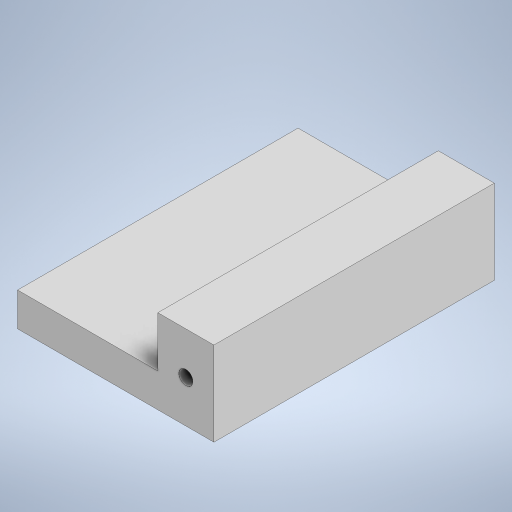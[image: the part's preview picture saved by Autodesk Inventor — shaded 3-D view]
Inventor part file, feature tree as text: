
AUTODESK INVENTOR PART (.ipt)
format: ipt  version: 2023 (Build 270158000, 158)  size: 227,328 bytes
history: native  units: in
note: dims shown in document units (in); Inventor stores cm internally (conversion verified against a paired STEP export)
features: extrude x3, sketch x3
ambient origin geometry x8: Origin, YZ Plane, XZ Plane, XY Plane, X Axis, Y Axis, Z Axis, Center Point
bodies: Body1 (feature_tree)
feature tree (6):
  extrude  "Extrusion2"  Depth=0.7874in
  extrude  "Extrusion4"  Depth=0.3937in
  extrude  "Extrusion5"  Depth=0.9843in TaperAngle=0.0deg
  sketch  "Sketch1"  dims[d0=1.1811in d1=0.7874in]
  sketch  "Sketch4"  dims[d5=0.3937in d6=0.5906in]
  sketch  "Sketch5"  dims[d7=0.1969in d8=0.9843in d9=0.0in d13=0.4724in d14=1.9685in d15=3.937in d16=0.0in d17=0.3543in d18=2.9528in d19=0.0in]
